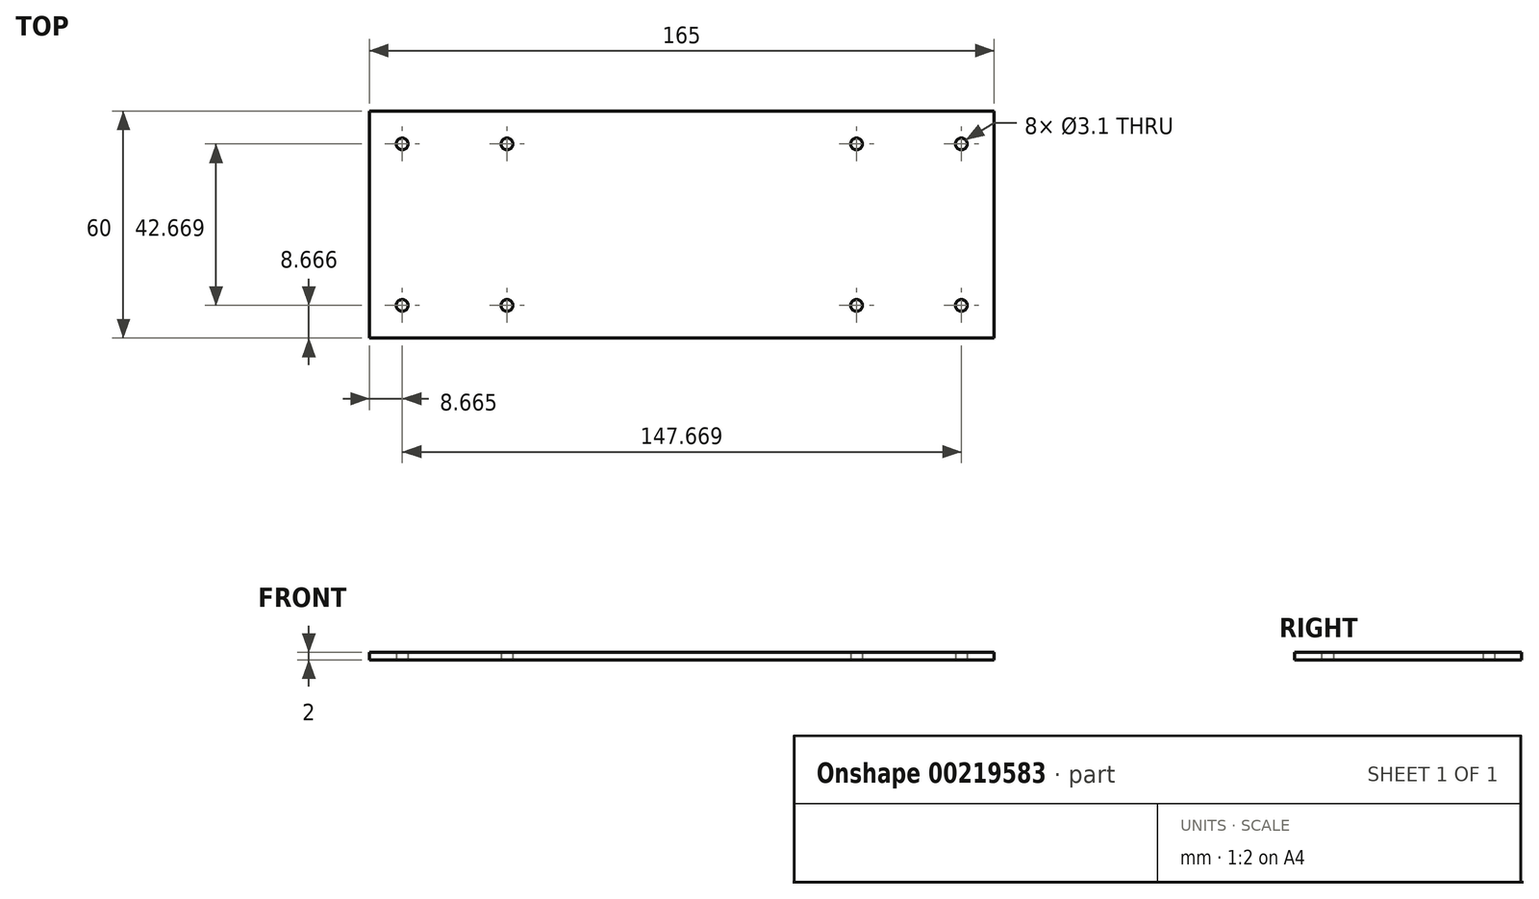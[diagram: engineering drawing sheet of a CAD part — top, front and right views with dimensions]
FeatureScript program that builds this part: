
annotation { "Feature Type Name" : "Feature", "Feature Type Description" : "" }
export const myFeature = defineFeature(function(context is Context, id is Id, definition is map)
    precondition{}
    {
        {
            var Q0;
            Q0=qCreatedBy(makeId("Top.planeOp"),FACE);
            var sketch = newSketch(context, id + "F0", { "sketchPlane" : qUnion([Q0])});
            skLineSegment(sketch, "E0.bottom", {"start": v(82.5, -30) * mm, "end": v(-82.5, -30) * mm});
            skLineSegment(sketch, "E0.top", {"start": v(82.5, 30) * mm, "end": v(-82.5, 30) * mm});
            skLineSegment(sketch, "E0.left", {"start": v(82.5, -30) * mm, "end": v(82.5, 30) * mm});
            skLineSegment(sketch, "E0.right", {"start": v(-82.5, -30) * mm, "end": v(-82.5, 30) * mm});
            skPoint(sketch, "E0.middle", {"position": v(0, 0) * mm});
            skCircle(sketch, "E1", {"center": v(-73.83, 21.33) * mm, "radius": 1.55 * mm});
            skCircle(sketch, "E2", {"center": v(73.83, 21.33) * mm, "radius": 1.55 * mm});
            skCircle(sketch, "E3", {"center": v(73.83, -21.33) * mm, "radius": 1.55 * mm});
            skCircle(sketch, "E4", {"center": v(-73.83, -21.33) * mm, "radius": 1.55 * mm});
            skLineSegment(sketch, "E5", {"start": v(73.83, -21.33) * mm, "end": v(73.83, -30) * mm, "construction": true});
            skLineSegment(sketch, "E6", {"start": v(73.83, 21.33) * mm, "end": v(73.83, 30) * mm, "construction": true});
            skLineSegment(sketch, "E7", {"start": v(73.83, -21.33) * mm, "end": v(82.5, -21.33) * mm, "construction": true});
            skLineSegment(sketch, "E8", {"start": v(-73.83, -21.33) * mm, "end": v(-46.17, -21.33) * mm, "construction": true});
            skLineSegment(sketch, "E9", {"start": v(73.83, -21.33) * mm, "end": v(46.17, -21.33) * mm, "construction": true});
            skLineSegment(sketch, "E10", {"start": v(73.83, 21.33) * mm, "end": v(46.17, 21.33) * mm, "construction": true});
            skLineSegment(sketch, "E11", {"start": v(-73.83, 21.33) * mm, "end": v(-46.17, 21.33) * mm, "construction": true});
            skCircle(sketch, "E12", {"center": v(-46.17, -21.33) * mm, "radius": 1.55 * mm});
            skCircle(sketch, "E13", {"center": v(-46.17, 21.33) * mm, "radius": 1.55 * mm});
            skCircle(sketch, "E14", {"center": v(46.17, 21.33) * mm, "radius": 1.55 * mm});
            skCircle(sketch, "E15", {"center": v(46.17, -21.33) * mm, "radius": 1.55 * mm});
            skSolve(sketch);
        }
        {
            var Q0;
            Q0 = qSketchRegion(id + "F0", true);
            extrude(context, id + "F1", {"entities" : qUnion([Q0]), "depth" : 2 * mm});
        }
    });
